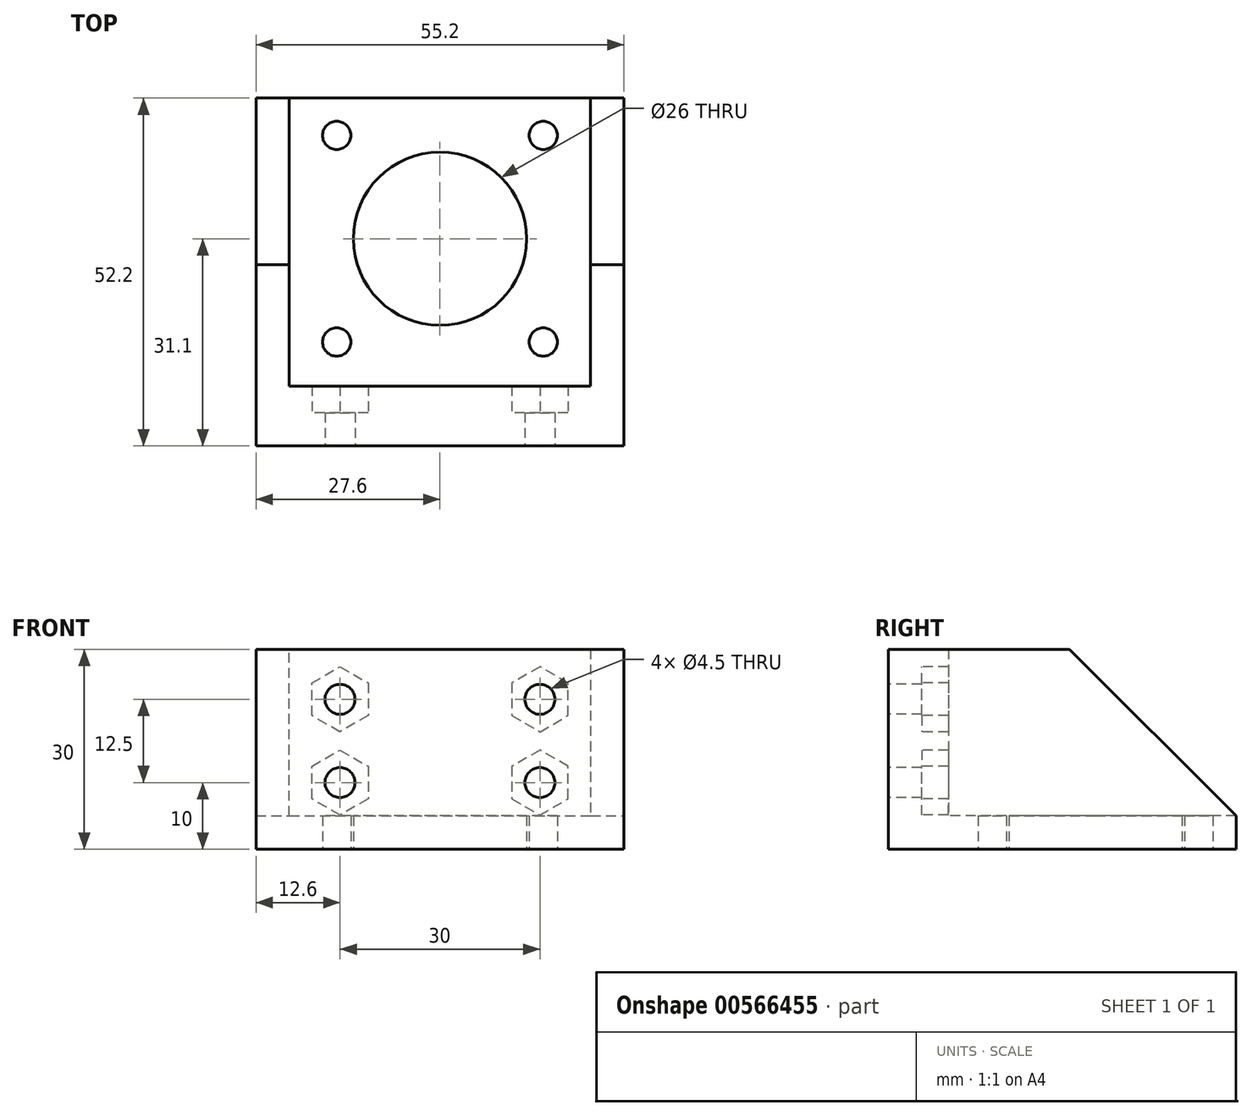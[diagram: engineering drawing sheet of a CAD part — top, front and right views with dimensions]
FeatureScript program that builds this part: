
annotation { "Feature Type Name" : "Feature", "Feature Type Description" : "" }
export const myFeature = defineFeature(function(context is Context, id is Id, definition is map)
    precondition{}
    {
        {
            var Q0;
            Q0=qCreatedBy(makeId("Top.planeOp"),FACE);
            var sketch = newSketch(context, id + "F0", { "sketchPlane" : qUnion([Q0])});
            skLineSegment(sketch, "E0.bottom", {"start": v(15.5, -15.5) * mm, "end": v(-15.5, -15.5) * mm, "construction": true});
            skLineSegment(sketch, "E0.top", {"start": v(15.5, 15.5) * mm, "end": v(-15.5, 15.5) * mm, "construction": true});
            skLineSegment(sketch, "E0.left", {"start": v(15.5, -15.5) * mm, "end": v(15.5, 15.5) * mm, "construction": true});
            skLineSegment(sketch, "E0.right", {"start": v(-15.5, -15.5) * mm, "end": v(-15.5, 15.5) * mm, "construction": true});
            skPoint(sketch, "E0.middle", {"position": v(0, 0) * mm});
            skCircle(sketch, "E1", {"center": v(-15.5, 15.5) * mm, "radius": 2.12 * mm});
            skCircle(sketch, "E2", {"center": v(15.5, 15.5) * mm, "radius": 2.12 * mm});
            skCircle(sketch, "E3", {"center": v(15.5, -15.5) * mm, "radius": 2.12 * mm});
            skCircle(sketch, "E4", {"center": v(-15.5, -15.5) * mm, "radius": 2.12 * mm});
            skCircle(sketch, "E5", {"center": v(0, 0) * mm, "radius": 13 * mm});
            skLineSegment(sketch, "E6.bottom", {"start": v(27.6, -21.1) * mm, "end": v(-27.6, -21.1) * mm, "construction": true});
            skLineSegment(sketch, "E6.top", {"start": v(27.6, 21.1) * mm, "end": v(-27.6, 21.1) * mm});
            skLineSegment(sketch, "E6.left", {"start": v(27.6, -21.1) * mm, "end": v(27.6, 21.1) * mm});
            skLineSegment(sketch, "E6.right", {"start": v(-27.6, -21.1) * mm, "end": v(-27.6, 21.1) * mm});
            skLineSegment(sketch, "E7", {"start": v(-27.6, -21.1) * mm, "end": v(-27.6, -31.1) * mm});
            skLineSegment(sketch, "E8", {"start": v(-27.6, -31.1) * mm, "end": v(0, -31.1) * mm});
            skLineSegment(sketch, "E9.MirrorCS", {"start": v(27.6, -21.1) * mm, "end": v(27.6, -31.1) * mm});
            skLineSegment(sketch, "E10.MirrorCS", {"start": v(27.6, -31.1) * mm, "end": v(0, -31.1) * mm});
            skSolve(sketch);
        }
        {
            var Q0;
            Q0=qSketchRegion(id+"F0",true);
            extrude(context, id + "F1", {"entities" : qUnion([Q0]), "depth" : 5 * mm, "offsetDistance" : 25 * mm});
        }
        {
            var Q0;
            Q0=makeQuery(id+"F1.opExtrude","CAP_FACE",FACE,{"disambiguationData":[OSD([sQuery(id+"F0.wireOp",EDGE,"E1"),sQuery(id+"F0.wireOp",EDGE,"E2"),sQuery(id+"F0.wireOp",EDGE,"E3"),sQuery(id+"F0.wireOp",EDGE,"E4"),sQuery(id+"F0.wireOp",EDGE,"E5"),sQuery(id+"F0.wireOp",EDGE,"E6.bottom"),sQuery(id+"F0.wireOp",EDGE,"E6.top"),sQuery(id+"F0.wireOp",EDGE,"E6.left"),sQuery(id+"F0.wireOp",EDGE,"E6.right")])],"isStart":false});
            var sketch = newSketch(context, id + "F2", { "sketchPlane" : qUnion([Q0])});
            skLineSegment(sketch, "E11.bottom", {"start": v(-22.6, 21.1) * mm, "end": v(-27.6, 21.1) * mm});
            skLineSegment(sketch, "E11.top", {"start": v(-22.6, -21.1) * mm, "end": v(-27.6, -21.1) * mm, "construction": true});
            skLineSegment(sketch, "E11.left", {"start": v(-22.6, 21.1) * mm, "end": v(-22.6, -21.1) * mm});
            skLineSegment(sketch, "E11.right", {"start": v(-27.6, 21.1) * mm, "end": v(-27.6, -21.1) * mm});
            skPoint(sketch, "E11.middle", {"position": v(-25.1, 0) * mm});
            skPoint(sketch, "E12.MirrorP", {"position": v(25.1, 0) * mm});
            skLineSegment(sketch, "E13.MirrorCS", {"start": v(22.6, 21.1) * mm, "end": v(27.6, 21.1) * mm});
            skLineSegment(sketch, "E14.MirrorCS", {"start": v(22.6, -21.1) * mm, "end": v(27.6, -21.1) * mm, "construction": true});
            skLineSegment(sketch, "E15.MirrorCS", {"start": v(22.6, 21.1) * mm, "end": v(22.6, -21.1) * mm});
            skLineSegment(sketch, "E16.MirrorCS", {"start": v(27.6, 21.1) * mm, "end": v(27.6, -21.1) * mm});
            skLineSegment(sketch, "E17", {"start": v(-27.6, -21.1) * mm, "end": v(-27.6, -31.1) * mm});
            skLineSegment(sketch, "E18", {"start": v(-27.6, -31.1) * mm, "end": v(-22.6, -31.1) * mm});
            skLineSegment(sketch, "E19", {"start": v(-22.6, -31.1) * mm, "end": v(-22.6, -21.1) * mm});
            skLineSegment(sketch, "E20", {"start": v(22.6, -21.1) * mm, "end": v(22.6, -31.1) * mm});
            skLineSegment(sketch, "E21", {"start": v(22.6, -31.1) * mm, "end": v(27.6, -31.1) * mm});
            skLineSegment(sketch, "E22", {"start": v(27.6, -31.1) * mm, "end": v(27.6, -21.1) * mm});
            skSolve(sketch);
        }
        {
            var Q0;
            Q0=qSketchRegion(id+"F2",true);
            extrude(context, id + "F3", {"entities" : qUnion([Q0]), "operationType" : NewBodyOperationType.ADD, "depth" : 25 * mm, "offsetDistance" : 25 * mm});
        }
        {
            var Q0;
            Q0=makeQuery(id+"F3.boolean.opBoolean","MERGE",FACE,{"derivedFrom":[makeQuery(id+"F1.opExtrude","SWEPT_FACE",FACE,{"disambiguationData":[OSD([sQuery(id+"F0.wireOp",EDGE,"E8"),sQuery(id+"F0.wireOp",EDGE,"E10.MirrorCS")])]}),makeQuery(id+"F3.opExtrude","SWEPT_FACE",FACE,{"disambiguationData":[OSD([sQuery(id+"F2.wireOp",EDGE,"E18")])]}),makeQuery(id+"F3.opExtrude","SWEPT_FACE",FACE,{"disambiguationData":[OSD([sQuery(id+"F2.wireOp",EDGE,"E21")])]})]});
            var sketch = newSketch(context, id + "F4", { "sketchPlane" : qUnion([Q0])});
            skLineSegment(sketch, "E23.bottom", {"start": v(-27.6, 30) * mm, "end": v(27.6, 30) * mm});
            skLineSegment(sketch, "E23.top", {"start": v(-27.6, 0) * mm, "end": v(27.6, 0) * mm});
            skLineSegment(sketch, "E23.left", {"start": v(-27.6, 30) * mm, "end": v(-27.6, 0) * mm});
            skLineSegment(sketch, "E23.right", {"start": v(27.6, 30) * mm, "end": v(27.6, 0) * mm});
            skCircle(sketch, "E24", {"center": v(-15, 22.5) * mm, "radius": 2.25 * mm});
            skCircle(sketch, "E25", {"center": v(-15, 10) * mm, "radius": 2.25 * mm});
            skCircle(sketch, "E26.MirrorC", {"center": v(15, 22.5) * mm, "radius": 2.25 * mm});
            skCircle(sketch, "E27.MirrorC", {"center": v(15, 10) * mm, "radius": 2.25 * mm});
            skSolve(sketch);
        }
        {
            var Q0;
            Q0=qSketchRegion(id+"F4",true);
            extrude(context, id + "F5", {"entities" : qUnion([Q0]), "operationType" : NewBodyOperationType.ADD, "oppositeDirection" : true, "depth" : 5 * mm, "offsetDistance" : 25 * mm});
        }
        {
            var Q0;
            Q0=makeQuery(id+"F5.opExtrude","CAP_FACE",FACE,{"disambiguationData":[OSD([sQuery(id+"F4.wireOp",EDGE,"E23.bottom"),sQuery(id+"F4.wireOp",EDGE,"E23.top"),sQuery(id+"F4.wireOp",EDGE,"E23.left"),sQuery(id+"F4.wireOp",EDGE,"E23.right"),sQuery(id+"F4.wireOp",EDGE,"E24"),sQuery(id+"F4.wireOp",EDGE,"E25"),sQuery(id+"F4.wireOp",EDGE,"E26.MirrorC"),sQuery(id+"F4.wireOp",EDGE,"E27.MirrorC")])],"isStart":false});
            var sketch = newSketch(context, id + "F6", { "sketchPlane" : qUnion([Q0])});
            skCircle(sketch, "E28.cCircle", {"center": v(-15, 22.5) * mm, "radius": 4.22 * mm, "construction": true});
            skLineSegment(sketch, "E28.0", {"start": v(-10.77, 24.94) * mm, "end": v(-10.77, 20.06) * mm});
            skLineSegment(sketch, "E28.1", {"start": v(-10.77, 20.06) * mm, "end": v(-15, 17.62) * mm});
            skLineSegment(sketch, "E28.2", {"start": v(-15, 17.62) * mm, "end": v(-19.22, 20.06) * mm});
            skLineSegment(sketch, "E28.3", {"start": v(-19.22, 20.06) * mm, "end": v(-19.22, 24.94) * mm});
            skLineSegment(sketch, "E28.4", {"start": v(-19.22, 24.94) * mm, "end": v(-15, 27.38) * mm});
            skLineSegment(sketch, "E28.5", {"start": v(-15, 27.38) * mm, "end": v(-10.77, 24.94) * mm});
            skPoint(sketch, "E28.0.midPoint", {"position": v(-10.77, 22.5) * mm});
            skCircle(sketch, "E29.cCircle", {"center": v(-15, 10) * mm, "radius": 4.22 * mm, "construction": true});
            skLineSegment(sketch, "E29.0", {"start": v(-10.77, 12.44) * mm, "end": v(-10.77, 7.56) * mm});
            skLineSegment(sketch, "E29.1", {"start": v(-10.77, 7.56) * mm, "end": v(-15, 5.12) * mm});
            skLineSegment(sketch, "E29.2", {"start": v(-15, 5.12) * mm, "end": v(-19.22, 7.56) * mm});
            skLineSegment(sketch, "E29.3", {"start": v(-19.22, 7.56) * mm, "end": v(-19.22, 12.44) * mm});
            skLineSegment(sketch, "E29.4", {"start": v(-19.22, 12.44) * mm, "end": v(-15, 14.88) * mm});
            skLineSegment(sketch, "E29.5", {"start": v(-15, 14.88) * mm, "end": v(-10.77, 12.44) * mm});
            skPoint(sketch, "E29.0.midPoint", {"position": v(-10.77, 10) * mm});
            skLineSegment(sketch, "E30.MirrorCS", {"start": v(10.77, 12.44) * mm, "end": v(10.77, 7.56) * mm});
            skLineSegment(sketch, "E31.MirrorCS", {"start": v(10.77, 7.56) * mm, "end": v(15, 5.12) * mm});
            skLineSegment(sketch, "E32.MirrorCS", {"start": v(15, 5.12) * mm, "end": v(19.22, 7.56) * mm});
            skLineSegment(sketch, "E33.MirrorCS", {"start": v(19.22, 7.56) * mm, "end": v(19.22, 12.44) * mm});
            skLineSegment(sketch, "E34.MirrorCS", {"start": v(15, 27.38) * mm, "end": v(10.77, 24.94) * mm});
            skLineSegment(sketch, "E35.MirrorCS", {"start": v(19.22, 20.06) * mm, "end": v(19.22, 24.94) * mm});
            skLineSegment(sketch, "E36.MirrorCS", {"start": v(15, 17.62) * mm, "end": v(19.22, 20.06) * mm});
            skLineSegment(sketch, "E37.MirrorCS", {"start": v(10.77, 20.06) * mm, "end": v(15, 17.62) * mm});
            skLineSegment(sketch, "E38.MirrorCS", {"start": v(10.77, 24.94) * mm, "end": v(10.77, 20.06) * mm});
            skLineSegment(sketch, "E39.MirrorCS", {"start": v(15, 14.88) * mm, "end": v(10.77, 12.44) * mm});
            skLineSegment(sketch, "E40.MirrorCS", {"start": v(19.22, 12.44) * mm, "end": v(15, 14.88) * mm});
            skPoint(sketch, "E41.MirrorP", {"position": v(10.77, 10) * mm});
            skPoint(sketch, "E42.MirrorP", {"position": v(10.77, 22.5) * mm});
            skCircle(sketch, "E43.MirrorC", {"center": v(15, 10) * mm, "radius": 4.22 * mm, "construction": true});
            skLineSegment(sketch, "E44.MirrorCS", {"start": v(19.22, 24.94) * mm, "end": v(15, 27.38) * mm});
            skCircle(sketch, "E45.MirrorC", {"center": v(15, 22.5) * mm, "radius": 4.22 * mm, "construction": true});
            skLineSegment(sketch, "E46.bottom", {"start": v(-22.6, 30) * mm, "end": v(22.6, 30) * mm});
            skLineSegment(sketch, "E46.top", {"start": v(-22.6, 5) * mm, "end": v(22.6, 5) * mm});
            skLineSegment(sketch, "E46.left", {"start": v(22.6, 30) * mm, "end": v(22.6, 5) * mm});
            skLineSegment(sketch, "E46.right", {"start": v(-22.6, 30) * mm, "end": v(-22.6, 5) * mm});
            skSolve(sketch);
        }
        {
            var Q0;
            Q0=qSketchRegion(id+"F6",true);
            extrude(context, id + "F7", {"entities" : qUnion([Q0]), "operationType" : NewBodyOperationType.ADD, "depth" : 4 * mm, "offsetDistance" : 25 * mm});
        }
        {
            var Q0;
            Q0=makeQuery(id+"F3.opExtrude","CAP_EDGE",EDGE,{"disambiguationData":[OSD([sQuery(id+"F2.wireOp",EDGE,"E11.bottom")])],"isStart":false});
            var Q1;
            Q1=makeQuery(id+"F3.opExtrude","CAP_EDGE",EDGE,{"disambiguationData":[OSD([sQuery(id+"F2.wireOp",EDGE,"E13.MirrorCS")])],"isStart":false});
            chamfer(context, id + "F8", {"entities" : qUnion([Q0, Q1]), "width" : 25 * mm, "tangentPropagation" : true});
        }
    });
